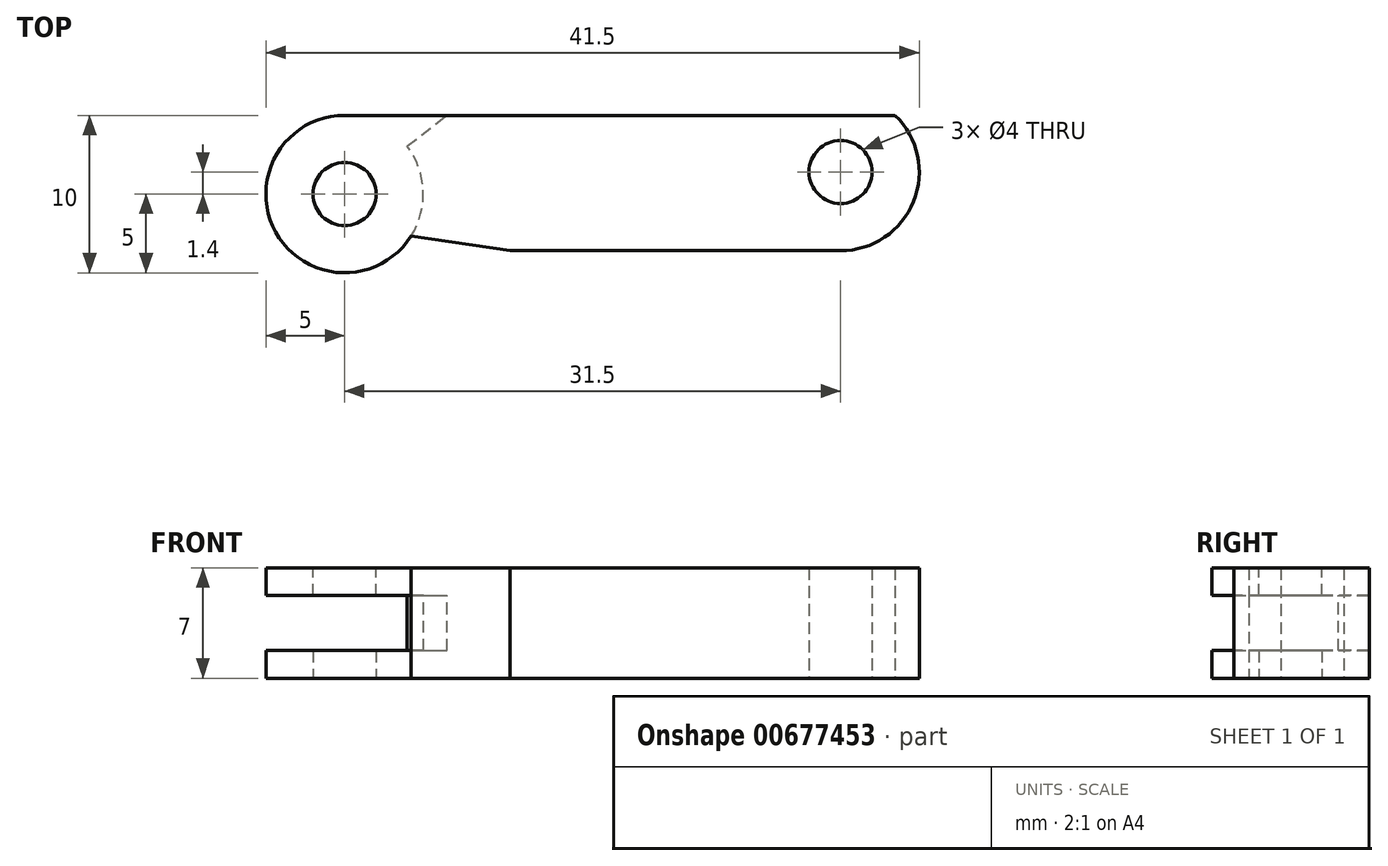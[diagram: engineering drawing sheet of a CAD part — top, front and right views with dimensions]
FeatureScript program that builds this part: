
annotation { "Feature Type Name" : "Feature", "Feature Type Description" : "" }
export const myFeature = defineFeature(function(context is Context, id is Id, definition is map)
    precondition{}
    {
        {
            var Q0;
            Q0=qCreatedBy(makeId("Top.planeOp"),FACE);
            var sketch = newSketch(context, id + "F0", { "sketchPlane" : qUnion([Q0])});
            skLineSegment(sketch, "E0", {"start": v(5.04, 0) * mm, "end": v(40, 0) * mm});
            skLineSegment(sketch, "E1", {"start": v(36.54, -8.6) * mm, "end": v(15.54, -8.6) * mm});
            skPoint(sketch, "E2", {"position": v(5.04, 0) * mm});
            skPoint(sketch, "E3", {"position": v(5.04, -5) * mm});
            skArc(sketch, "E4", {"start": v(5.04, 0) * mm, "mid": v(0.66, -7.42) * mm, "end": v(9.27, -7.66) * mm});
            skPoint(sketch, "E5", {"position": v(36.54, -8.6) * mm});
            skPoint(sketch, "E6", {"position": v(36.54, -3.6) * mm});
            skArc(sketch, "E7", {"start": v(36.54, -8.6) * mm, "mid": v(41.18, -5.47) * mm, "end": v(40, 0) * mm});
            skPoint(sketch, "E8", {"position": v(15.54, -8.6) * mm});
            skCircle(sketch, "E9", {"center": v(5.04, -5) * mm, "radius": 2 * mm});
            skCircle(sketch, "E10", {"center": v(36.54, -3.6) * mm, "radius": 2 * mm});
            skPoint(sketch, "E11", {"position": v(0.04, -5) * mm});
            skPoint(sketch, "E12", {"position": v(41.54, -3.6) * mm});
            skLineSegment(sketch, "E13", {"start": v(15.54, -8.6) * mm, "end": v(9.27, -7.66) * mm});
            skSolve(sketch);
        }
        {
            var Q0;
            Q0=makeQuery(id+"F0.imprint","IMPRINT",FACE,{"disambiguationData":[TD([[makeQuery(id+"F0.imprint","IMPRINT",EDGE,{"derivedFrom":sQuery(id+"F0.wireOp",EDGE,"E0")}),-1.0]])]});
            extrude(context, id + "F1", {"entities" : qUnion([Q0]), "depth" : 7 * mm, "offsetDistance" : 25 * mm});
        }
        {
            var Q0;
            Q0=makeQuery(id+"F1.opExtrude","CAP_FACE",FACE,{"disambiguationData":[OSD([sQuery(id+"F0.wireOp",EDGE,"E0"),sQuery(id+"F0.wireOp",EDGE,"E1"),sQuery(id+"F0.wireOp",EDGE,"E4"),sQuery(id+"F0.wireOp",EDGE,"E7"),sQuery(id+"F0.wireOp",EDGE,"N5DSWfwR-mDIy-DwBs-O2GE-EQuleGf2mXDJ"),sQuery(id+"F0.wireOp",EDGE,"E9"),sQuery(id+"F0.wireOp",EDGE,"E10")])],"isStart":false});
            var sketch = newSketch(context, id + "F2", { "sketchPlane" : qUnion([Q0])});
            skArc(sketch, "E14", {"start": v(5.04, 0) * mm, "mid": v(2.83, -9.49) * mm, "end": v(9, -1.95) * mm});
            skLineSegment(sketch, "E15", {"start": v(9, -1.95) * mm, "end": v(11.54, 0) * mm});
            skLineSegment(sketch, "E16", {"start": v(11.54, 0) * mm, "end": v(5.04, 0) * mm});
            skSolve(sketch);
        }
        {
            var Q0;
            Q0 = qSketchRegion(id + "F2", true);
            extrude(context, id + "F3", {"entities" : qUnion([Q0]), "operationType" : NewBodyOperationType.REMOVE, "oppositeDirection" : true, "depth" : 5.25 * mm, "offsetDistance" : 25 * mm});
        }
        {
            var Q0;
            Q0 = qSketchRegion(id + "F2", true);
            extrude(context, id + "F4", {"entities" : qUnion([Q0]), "operationType" : NewBodyOperationType.ADD, "oppositeDirection" : true, "depth" : 1.75 * mm, "offsetDistance" : 25 * mm});
        }
        {
            var Q0;
            Q0=makeQuery(id+"F4.boolean.opBoolean","MERGE",FACE,{"derivedFrom":[makeQuery(id+"F1.opExtrude","CAP_FACE",FACE,{"disambiguationData":[OSD([sQuery(id+"F0.wireOp",EDGE,"E0"),sQuery(id+"F0.wireOp",EDGE,"E1"),sQuery(id+"F0.wireOp",EDGE,"E4"),sQuery(id+"F0.wireOp",EDGE,"E7"),sQuery(id+"F0.wireOp",EDGE,"N5DSWfwR-mDIy-DwBs-O2GE-EQuleGf2mXDJ"),sQuery(id+"F0.wireOp",EDGE,"E9"),sQuery(id+"F0.wireOp",EDGE,"E10")])],"isStart":false}),makeQuery(id+"F4.opExtrude","CAP_FACE",FACE,{"disambiguationData":[OSD([sQuery(id+"F2.wireOp",EDGE,"E14")])],"isStart":true})]});
            var sketch = newSketch(context, id + "F5", { "sketchPlane" : qUnion([Q0])});
            skCircle(sketch, "E17", {"center": v(5.04, -5) * mm, "radius": 2 * mm});
            skSolve(sketch);
        }
        {
            var Q0;
            Q0 = qSketchRegion(id + "F5", true);
            extrude(context, id + "F6", {"entities" : qUnion([Q0]), "operationType" : NewBodyOperationType.REMOVE, "oppositeDirection" : true, "depth" : 1.75 * mm, "offsetDistance" : 25 * mm});
        }
    });
